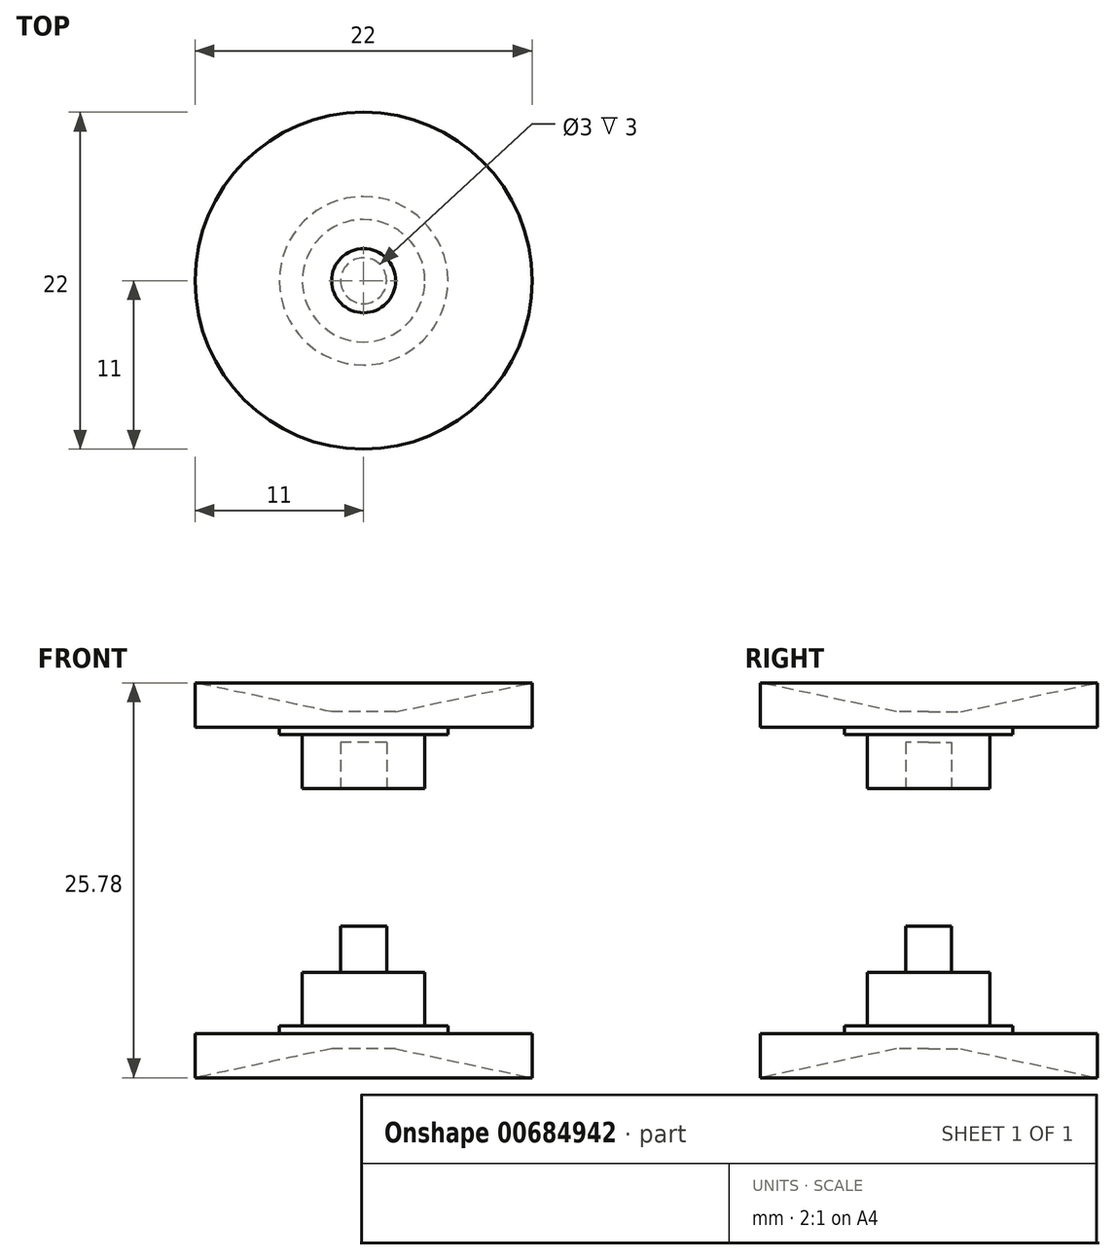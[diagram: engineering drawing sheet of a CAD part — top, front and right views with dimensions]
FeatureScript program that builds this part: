
annotation { "Feature Type Name" : "Feature", "Feature Type Description" : "" }
export const myFeature = defineFeature(function(context is Context, id is Id, definition is map)
    precondition{}
    {
        {
            var Q0;
            Q0=qCreatedBy(makeId("Top.planeOp"),FACE);
            var sketch = newSketch(context, id + "F0", { "sketchPlane" : qUnion([Q0])});
            skCircle(sketch, "E0", {"center": v(0, 0) * mm, "radius": 11 * mm});
            skCircle(sketch, "E1", {"center": v(0, 0) * mm, "radius": 5.5 * mm});
            skCircle(sketch, "E2", {"center": v(0, 0) * mm, "radius": 4 * mm});
            skCircle(sketch, "E3", {"center": v(0, 0) * mm, "radius": 1.5 * mm});
            skSolve(sketch);
        }
        {
            var Q0;
            Q0=makeQuery(id+"F0.imprint","IMPRINT",FACE,{"disambiguationData":[TD([[makeQuery(id+"F0.imprint","IMPRINT",EDGE,{"derivedFrom":sQuery(id+"F0.wireOp",EDGE,"E0")}),1.0]])]});
            var Q1;
            Q1=makeQuery(id+"F0.imprint","IMPRINT",FACE,{"disambiguationData":[TD([[makeQuery(id+"F0.imprint","IMPRINT",EDGE,{"derivedFrom":sQuery(id+"F0.wireOp",EDGE,"E1")}),1.0]])]});
            var Q2;
            Q2=makeQuery(id+"F0.imprint","IMPRINT",FACE,{"disambiguationData":[TD([[makeQuery(id+"F0.imprint","IMPRINT",EDGE,{"derivedFrom":sQuery(id+"F0.wireOp",EDGE,"E2")}),1.0]])]});
            var Q3;
            Q3=makeQuery(id+"F0.imprint","IMPRINT",FACE,{"disambiguationData":[TD([[makeQuery(id+"F0.imprint","IMPRINT",EDGE,{"derivedFrom":sQuery(id+"F0.wireOp",EDGE,"E3")}),1.0]])]});
            extrude(context, id + "F1", {"entities" : qUnion([Q0, Q1, Q2, Q3]), "depth" : 1 * mm, "offsetDistance" : 25 * mm});
        }
        {
            var Q0;
            Q0=makeQuery(id+"F0.imprint","IMPRINT",FACE,{"disambiguationData":[TD([[makeQuery(id+"F0.imprint","IMPRINT",EDGE,{"derivedFrom":sQuery(id+"F0.wireOp",EDGE,"E1")}),1.0]])]});
            extrude(context, id + "F2", {"entities" : qUnion([Q0]), "operationType" : NewBodyOperationType.ADD, "depth" : 1.5 * mm, "offsetDistance" : 25 * mm, "hasSecondDirection" : true, "secondDirectionBound" : SecondDirectionBoundingType.UP_TO_NEXT, "secondDirectionOppositeDirection" : false, "secondDirectionDepth" : 25 * mm});
        }
        {
            var Q0;
            Q0=makeQuery(id+"F0.imprint","IMPRINT",FACE,{"disambiguationData":[TD([[makeQuery(id+"F0.imprint","IMPRINT",EDGE,{"derivedFrom":sQuery(id+"F0.wireOp",EDGE,"E2")}),1.0]])]});
            extrude(context, id + "F3", {"entities" : qUnion([Q0]), "operationType" : NewBodyOperationType.ADD, "depth" : 5 * mm, "offsetDistance" : 25 * mm});
        }
        {
            var Q0;
            Q0=makeQuery(id+"F0.imprint","IMPRINT",FACE,{"disambiguationData":[TD([[makeQuery(id+"F0.imprint","IMPRINT",EDGE,{"derivedFrom":sQuery(id+"F0.wireOp",EDGE,"E3")}),1.0]])]});
            extrude(context, id + "F4", {"entities" : qUnion([Q0]), "operationType" : NewBodyOperationType.ADD, "depth" : 8 * mm, "offsetDistance" : 25 * mm});
        }
        {
            var Q0;
            Q0=makeQuery(id+"F0.imprint","IMPRINT",FACE,{"disambiguationData":[TD([[makeQuery(id+"F0.imprint","IMPRINT",EDGE,{"derivedFrom":sQuery(id+"F0.wireOp",EDGE,"E0")}),1.0]])]});
            var Q1;
            Q1=makeQuery(id+"F0.imprint","IMPRINT",FACE,{"disambiguationData":[TD([[makeQuery(id+"F0.imprint","IMPRINT",EDGE,{"derivedFrom":sQuery(id+"F0.wireOp",EDGE,"E1")}),1.0]])]});
            var Q2;
            Q2=makeQuery(id+"F0.imprint","IMPRINT",FACE,{"disambiguationData":[TD([[makeQuery(id+"F0.imprint","IMPRINT",EDGE,{"derivedFrom":sQuery(id+"F0.wireOp",EDGE,"E2")}),1.0]])]});
            extrude(context, id + "F5", {"entities" : qUnion([Q0, Q1, Q2]), "operationType" : NewBodyOperationType.ADD, "oppositeDirection" : true, "depth" : 2 * mm, "offsetDistance" : 25 * mm});
        }
        {
            var Q0;
            Q0=makeQuery(id+"F5.opExtrude","CAP_EDGE",EDGE,{"disambiguationData":[OSD([sQuery(id+"F0.wireOp",EDGE,"E3")])],"isStart":false});
            chamfer(context, id + "F6", {"entities" : qUnion([Q0]), "chamferType" : ChamferType.OFFSET_ANGLE, "width" : 10 * mm, "oppositeDirection" : false, "angle" : 12 * degree, "tangentPropagation" : true});
        }
        {
            var Q0;
            Q0=makeQuery(id+"F1.opExtrude","CAP_FACE",FACE,{"disambiguationData":[OSD([sQuery(id+"F0.wireOp",EDGE,"E0"),sQuery(id+"F0.wireOp",EDGE,"E1")])],"isStart":false});
            cPlane(context, id + "F7", {"entities" : qUnion([Q0]), "cplaneType" : CPlaneType.OFFSET, "offset" : 10 * mm, "width" : 150 * mm, "height" : 150 * mm});
        }
        {
            var Q0;
            Q0=makeQuery(id+"F1.opExtrude","SWEPT_BODY",BODY,{"disambiguationData":[OSD([sQuery(id+"F0.wireOp",EDGE,"E0"),sQuery(id+"F0.wireOp",EDGE,"E1")])]});
            var Q1;
            Q1=qCreatedBy(id+"F7.planeOp",FACE);
            mirror(context, id + "F8", {"entities" : qUnion([Q0]), "mirrorPlane" : qUnion([Q1])});
        }
        {
            var Q0;
            Q0=makeQuery(id+"F8.opPattern","COPY",FACE,{"derivedFrom":makeQuery(id+"F4.opExtrude","CAP_FACE",FACE,{"disambiguationData":[OSD([sQuery(id+"F0.wireOp",EDGE,"E3")])],"isStart":false}),"instanceName":"1"});
            extrude(context, id + "F9", {"entities" : qUnion([Q0]), "operationType" : NewBodyOperationType.REMOVE, "oppositeDirection" : true, "depth" : 6 * mm, "offsetDistance" : 25 * mm});
        }
    });
